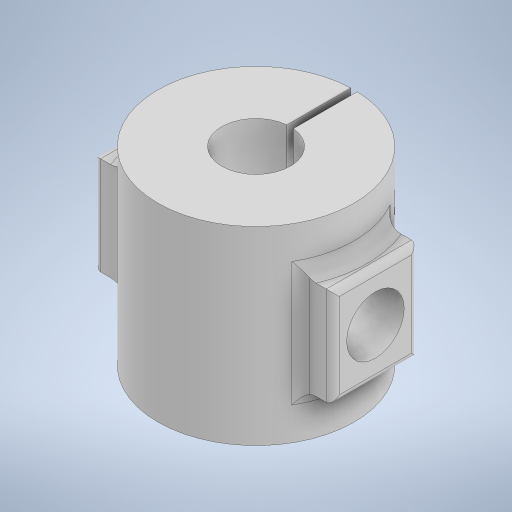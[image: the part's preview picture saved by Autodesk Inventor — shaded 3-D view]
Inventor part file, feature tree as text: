
AUTODESK INVENTOR PART (.ipt)
format: ipt  version: 2023 (Build 270158030, 158C)  size: 335,872 bytes
history: native  units: in
note: dims shown in document units (in); Inventor stores cm internally (conversion verified against a paired STEP export)
features: sketch x4, extrude x2, hole x2, fillet x2, plane x1, mirror x1
ambient origin geometry x8: Origin, YZ Plane, XZ Plane, XY Plane, X Axis, Y Axis, Z Axis, Center Point
bodies: Solid1 (feature_tree)
feature tree (12):
  extrude  "Extrusion1"  Depth=0.4134in
  plane  "Work Plane2"
  hole  "Hole1"  [1 undecoded]
  mirror  "Mirror1"
  extrude  "Extrusion2"  Depth=0.1575in
  hole  "Hole3"  [1 undecoded]
  fillet  "Fillet1"  Radius=0.5906in
  fillet  "Fillet2"  Radius=0.0787in
  sketch  "Sketch1"  dims[d0=1.1811in d1=0.4134in]
  sketch  "Sketch3"  dims[d2=0.0394in d3=1.1417in d4=0.0in]
  sketch  "Sketch5"  dims[d6=0.2953in d7=0.1575in]
  sketch  "Sketch6"  dims[d8=0.1102in d9=0.2362in d10=0.2362in d11=0.3543in d12=90.0deg d13=0.315in d14=0.8108in d23=0.5118in d25=0.5906in d26=0.0in d27=0.3465in d28=0.2362in d29=0.1575in d30=0.0787in d31=90.0deg d32=0.3543in d33=0.0in d34=0.0787in d35=0.0394in d36=0.5118in]
note: 2 required parameter values undecoded (feature->parameter linkage not recoverable at this tier; creation-order binding heuristic only, values carry confidence <= 0.55)
